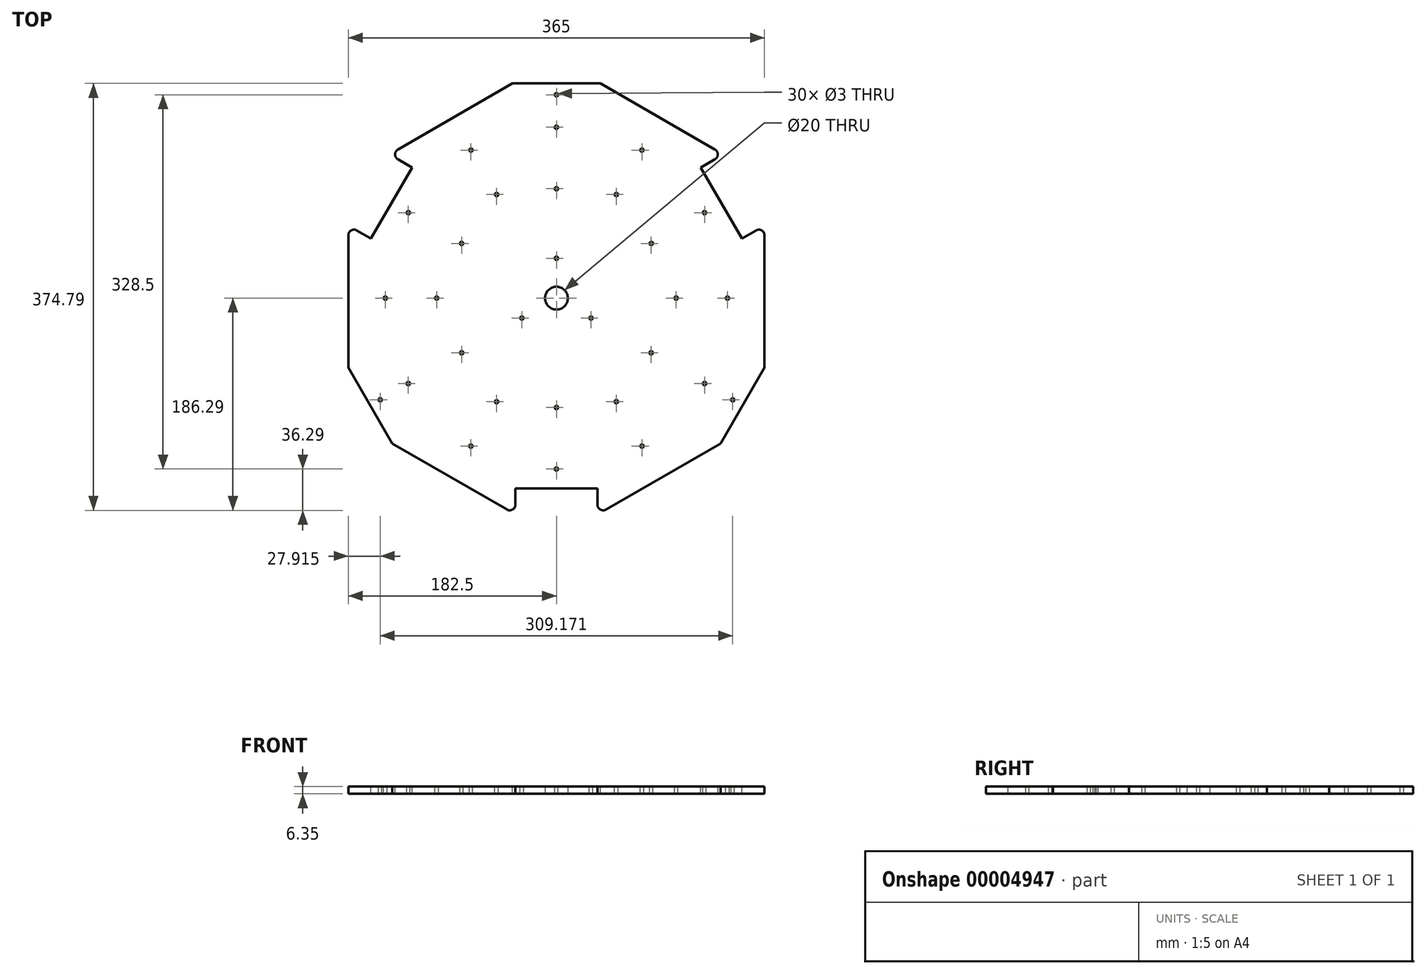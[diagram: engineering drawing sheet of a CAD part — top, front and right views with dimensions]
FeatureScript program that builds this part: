
annotation { "Feature Type Name" : "Feature", "Feature Type Description" : "" }
export const myFeature = defineFeature(function(context is Context, id is Id, definition is map)
    precondition{}
    {
        {
            var Q0;
            Q0=qCreatedBy(makeId("Top.planeOp"),FACE);
            var sketch = newSketch(context, id + "F0", { "sketchPlane" : qUnion([Q0])});
            skCircle(sketch, "E0", {"center": v(0, 0) * mm, "radius": 210.73 * mm, "construction": true});
            skLineSegment(sketch, "E1", {"start": v(0, 210.73) * mm, "end": v(0, 0) * mm, "construction": true});
            skLineSegment(sketch, "E2", {"start": v(0, 0) * mm, "end": v(-182.5, 105.37) * mm, "construction": true});
            skLineSegment(sketch, "E3", {"start": v(-182.5, 105.37) * mm, "end": v(0, 210.73) * mm});
            skLineSegment(sketch, "E4.1.0", {"start": v(-182.5, -105.37) * mm, "end": v(-182.5, 105.37) * mm});
            skLineSegment(sketch, "E4.2.0", {"start": v(0, -210.73) * mm, "end": v(-182.5, -105.37) * mm});
            skLineSegment(sketch, "E4.3.0", {"start": v(182.5, -105.37) * mm, "end": v(0, -210.73) * mm});
            skLineSegment(sketch, "E4.4.0", {"start": v(182.5, 105.37) * mm, "end": v(182.5, -105.37) * mm});
            skLineSegment(sketch, "E4.5.0", {"start": v(0, 210.73) * mm, "end": v(182.5, 105.37) * mm});
            skCircle(sketch, "E5", {"center": v(0, 0) * mm, "radius": 10 * mm});
            skSolve(sketch);
        }
        {
            var Q0;
            Q0 = qSketchRegion(id + "F0", true);
            extrude(context, id + "F1", {"entities" : qUnion([Q0]), "depth" : 6.35 * mm});
        }
        {
            var Q0;
            Q0=makeQuery(id+"F1.opExtrude","CAP_FACE",FACE,{"disambiguationData":[OSD([sQuery(id+"F0.wireOp",EDGE,"E3"),sQuery(id+"F0.wireOp",EDGE,"E4.1.0"),sQuery(id+"F0.wireOp",EDGE,"E4.2.0"),sQuery(id+"F0.wireOp",EDGE,"E4.3.0"),sQuery(id+"F0.wireOp",EDGE,"E4.4.0"),sQuery(id+"F0.wireOp",EDGE,"E4.5.0"),sQuery(id+"F0.wireOp",EDGE,"E5")])],"isStart":false});
            var sketch = newSketch(context, id + "F2", { "sketchPlane" : qUnion([Q0])});
            skLineSegment(sketch, "E6", {"start": v(0, 0) * mm, "end": v(182.5, 0) * mm, "construction": true});
            skLineSegment(sketch, "E7", {"start": v(-38.5, 188.5) * mm, "end": v(38.5, 188.5) * mm});
            skPoint(sketch, "E8", {"position": v(0, 188.5) * mm});
            skLineSegment(sketch, "E9", {"start": v(-38.5, 188.5) * mm, "end": v(0, 210.73) * mm});
            skLineSegment(sketch, "E10", {"start": v(0, 210.73) * mm, "end": v(38.5, 188.5) * mm});
            skLineSegment(sketch, "E11.1.0", {"start": v(-182.5, 60.9) * mm, "end": v(-182.5, 105.37) * mm});
            skLineSegment(sketch, "E11.1.1", {"start": v(-182.5, 105.37) * mm, "end": v(-144, 127.6) * mm});
            skLineSegment(sketch, "E11.1.2", {"start": v(-182.5, 60.9) * mm, "end": v(-144, 127.6) * mm});
            skPoint(sketch, "E11.1.3", {"position": v(-163.25, 94.25) * mm});
            skLineSegment(sketch, "E11.2.0", {"start": v(-144, -127.6) * mm, "end": v(-182.5, -105.37) * mm});
            skLineSegment(sketch, "E11.2.1", {"start": v(-182.5, -105.37) * mm, "end": v(-182.5, -60.9) * mm});
            skLineSegment(sketch, "E11.2.2", {"start": v(-144, -127.6) * mm, "end": v(-182.5, -60.9) * mm});
            skPoint(sketch, "E11.2.3", {"position": v(-163.25, -94.25) * mm});
            skLineSegment(sketch, "E11.3.0", {"start": v(38.5, -188.5) * mm, "end": v(0, -210.73) * mm});
            skLineSegment(sketch, "E11.3.1", {"start": v(0, -210.73) * mm, "end": v(-38.5, -188.5) * mm});
            skLineSegment(sketch, "E11.3.2", {"start": v(38.5, -188.5) * mm, "end": v(-38.5, -188.5) * mm});
            skPoint(sketch, "E11.3.3", {"position": v(0, -188.5) * mm});
            skLineSegment(sketch, "E11.4.0", {"start": v(182.5, -60.9) * mm, "end": v(182.5, -105.37) * mm});
            skLineSegment(sketch, "E11.4.1", {"start": v(182.5, -105.37) * mm, "end": v(144, -127.6) * mm});
            skLineSegment(sketch, "E11.4.2", {"start": v(182.5, -60.9) * mm, "end": v(144, -127.6) * mm});
            skPoint(sketch, "E11.4.3", {"position": v(163.25, -94.25) * mm});
            skLineSegment(sketch, "E11.5.0", {"start": v(144, 127.6) * mm, "end": v(182.5, 105.37) * mm});
            skLineSegment(sketch, "E11.5.1", {"start": v(182.5, 105.37) * mm, "end": v(182.5, 60.9) * mm});
            skLineSegment(sketch, "E11.5.2", {"start": v(144, 127.6) * mm, "end": v(182.5, 60.9) * mm});
            skPoint(sketch, "E11.5.3", {"position": v(163.25, 94.25) * mm});
            skPoint(sketch, "E11.center", {"position": v(0, 0) * mm});
            skSolve(sketch);
        }
        {
            var Q0;
            Q0 = qSketchRegion(id + "F2", true);
            extrude(context, id + "F3", {"entities" : qUnion([Q0]), "operationType" : NewBodyOperationType.REMOVE, "endBound" : BoundingType.THROUGH_ALL, "oppositeDirection" : true, "depth" : 25 * mm});
        }
        {
            var Q0;
            Q0=makeQuery(id+"F1.opExtrude","CAP_FACE",FACE,{"disambiguationData":[OSD([sQuery(id+"F0.wireOp",EDGE,"E3"),sQuery(id+"F0.wireOp",EDGE,"E4.1.0"),sQuery(id+"F0.wireOp",EDGE,"E4.2.0"),sQuery(id+"F0.wireOp",EDGE,"E4.3.0"),sQuery(id+"F0.wireOp",EDGE,"E4.4.0"),sQuery(id+"F0.wireOp",EDGE,"E4.5.0"),sQuery(id+"F0.wireOp",EDGE,"E5")])],"isStart":false});
            var sketch = newSketch(context, id + "F4", { "sketchPlane" : qUnion([Q0])});
            skLineSegment(sketch, "E12", {"start": v(0, 188.5) * mm, "end": v(0, 0) * mm, "construction": true});
            skLineSegment(sketch, "E13", {"start": v(0, 0) * mm, "end": v(-163.25, -94.25) * mm, "construction": true});
            skLineSegment(sketch, "E14", {"start": v(0, 0) * mm, "end": v(163.25, -94.25) * mm, "construction": true});
            skCircle(sketch, "E15", {"center": v(0, 178.5) * mm, "radius": 1.5 * mm});
            skCircle(sketch, "E16", {"center": v(0, 35) * mm, "radius": 1.5 * mm});
            skCircle(sketch, "E17", {"center": v(0, 0) * mm, "radius": 25 * mm, "construction": true});
            skPoint(sketch, "E18", {"position": v(0, 25) * mm});
            skCircle(sketch, "E19.1.0", {"center": v(-30.31, -17.5) * mm, "radius": 1.5 * mm});
            skCircle(sketch, "E19.1.1", {"center": v(-154.59, -89.25) * mm, "radius": 1.5 * mm});
            skCircle(sketch, "E19.2.0", {"center": v(30.31, -17.5) * mm, "radius": 1.5 * mm});
            skCircle(sketch, "E19.2.1", {"center": v(154.59, -89.25) * mm, "radius": 1.5 * mm});
            skSolve(sketch);
        }
        {
            var Q0;
            Q0 = qSketchRegion(id + "F4", true);
            extrude(context, id + "F5", {"entities" : qUnion([Q0]), "operationType" : NewBodyOperationType.REMOVE, "endBound" : BoundingType.THROUGH_ALL, "oppositeDirection" : true, "depth" : 25 * mm});
        }
        {
            var Q0;
            Q0=makeQuery(id+"F1.opExtrude","CAP_FACE",FACE,{"disambiguationData":[OSD([sQuery(id+"F0.wireOp",EDGE,"E3"),sQuery(id+"F0.wireOp",EDGE,"E4.1.0"),sQuery(id+"F0.wireOp",EDGE,"E4.2.0"),sQuery(id+"F0.wireOp",EDGE,"E4.3.0"),sQuery(id+"F0.wireOp",EDGE,"E4.4.0"),sQuery(id+"F0.wireOp",EDGE,"E4.5.0"),sQuery(id+"F0.wireOp",EDGE,"E5")])],"isStart":false});
            var sketch = newSketch(context, id + "F6", { "sketchPlane" : qUnion([Q0])});
            skLineSegment(sketch, "E20", {"start": v(0, 0) * mm, "end": v(163.25, 94.25) * mm, "construction": true});
            skLineSegment(sketch, "E21", {"start": v(106.75, 149.1) * mm, "end": v(182.5, 17.9) * mm});
            skLineSegment(sketch, "E22.0", {"start": v(144, 127.6) * mm, "end": v(182.5, 60.9) * mm});
            skLineSegment(sketch, "E23", {"start": v(106.75, 149.1) * mm, "end": v(144, 127.6) * mm});
            skLineSegment(sketch, "E24", {"start": v(182.5, 60.9) * mm, "end": v(182.5, 17.9) * mm});
            skLineSegment(sketch, "E25.1.0", {"start": v(-144, 127.6) * mm, "end": v(-106.75, 149.1) * mm});
            skLineSegment(sketch, "E25.1.1", {"start": v(-182.5, 17.9) * mm, "end": v(-182.5, 60.9) * mm});
            skLineSegment(sketch, "E25.1.2", {"start": v(-182.5, 17.9) * mm, "end": v(-106.75, 149.1) * mm});
            skLineSegment(sketch, "E25.1.3", {"start": v(-182.5, 60.9) * mm, "end": v(-144, 127.6) * mm});
            skLineSegment(sketch, "E25.2.0", {"start": v(-38.5, -188.5) * mm, "end": v(-75.75, -167) * mm});
            skLineSegment(sketch, "E25.2.1", {"start": v(75.75, -167) * mm, "end": v(38.5, -188.5) * mm});
            skLineSegment(sketch, "E25.2.2", {"start": v(75.75, -167) * mm, "end": v(-75.75, -167) * mm});
            skLineSegment(sketch, "E25.2.3", {"start": v(38.5, -188.5) * mm, "end": v(-38.5, -188.5) * mm});
            skPoint(sketch, "E25.center", {"position": v(0, 0) * mm});
            skSolve(sketch);
        }
        {
            var Q0;
            Q0 = qSketchRegion(id + "F6", true);
            extrude(context, id + "F7", {"entities" : qUnion([Q0]), "operationType" : NewBodyOperationType.REMOVE, "endBound" : BoundingType.THROUGH_ALL, "oppositeDirection" : true, "depth" : 25 * mm});
        }
        {
            var Q0;
            Q0=makeQuery(id+"F1.opExtrude","CAP_FACE",FACE,{"disambiguationData":[OSD([sQuery(id+"F0.wireOp",EDGE,"E3"),sQuery(id+"F0.wireOp",EDGE,"E4.1.0"),sQuery(id+"F0.wireOp",EDGE,"E4.2.0"),sQuery(id+"F0.wireOp",EDGE,"E4.3.0"),sQuery(id+"F0.wireOp",EDGE,"E4.4.0"),sQuery(id+"F0.wireOp",EDGE,"E4.5.0"),sQuery(id+"F0.wireOp",EDGE,"E5")])],"isStart":false});
            var sketch = newSketch(context, id + "F8", { "sketchPlane" : qUnion([Q0])});
            skLineSegment(sketch, "E26", {"start": v(0, 0) * mm, "end": v(144.63, 83.5) * mm, "construction": true});
            skLineSegment(sketch, "E27", {"start": v(106.75, 149.1) * mm, "end": v(146.5, 126.15) * mm});
            skLineSegment(sketch, "E28", {"start": v(146.5, 126.15) * mm, "end": v(126.63, 114.68) * mm});
            skLineSegment(sketch, "E29", {"start": v(126.63, 114.68) * mm, "end": v(106.75, 149.1) * mm});
            skLineSegment(sketch, "E30.0.MirrorCS", {"start": v(182.5, 17.9) * mm, "end": v(182.5, 63.8) * mm});
            skLineSegment(sketch, "E30.1.MirrorCS", {"start": v(162.63, 52.32) * mm, "end": v(182.5, 17.9) * mm});
            skLineSegment(sketch, "E30.2.MirrorCS", {"start": v(182.5, 63.8) * mm, "end": v(162.63, 52.32) * mm});
            skLineSegment(sketch, "E31.1.0", {"start": v(-162.63, 52.32) * mm, "end": v(-182.5, 17.9) * mm});
            skLineSegment(sketch, "E31.1.1", {"start": v(-182.5, 17.9) * mm, "end": v(-182.5, 63.8) * mm});
            skLineSegment(sketch, "E31.1.2", {"start": v(-182.5, 63.8) * mm, "end": v(-162.63, 52.32) * mm});
            skLineSegment(sketch, "E31.1.3", {"start": v(-106.75, 149.1) * mm, "end": v(-146.5, 126.15) * mm});
            skLineSegment(sketch, "E31.1.4", {"start": v(-126.63, 114.68) * mm, "end": v(-106.75, 149.1) * mm});
            skLineSegment(sketch, "E31.1.5", {"start": v(-146.5, 126.15) * mm, "end": v(-126.63, 114.68) * mm});
            skLineSegment(sketch, "E31.2.0", {"start": v(36, -167) * mm, "end": v(75.75, -167) * mm});
            skLineSegment(sketch, "E31.2.1", {"start": v(75.75, -167) * mm, "end": v(36, -189.95) * mm});
            skLineSegment(sketch, "E31.2.2", {"start": v(36, -189.95) * mm, "end": v(36, -167) * mm});
            skLineSegment(sketch, "E31.2.3", {"start": v(-75.75, -167) * mm, "end": v(-36, -189.95) * mm});
            skLineSegment(sketch, "E31.2.4", {"start": v(-36, -167) * mm, "end": v(-75.75, -167) * mm});
            skLineSegment(sketch, "E31.2.5", {"start": v(-36, -189.95) * mm, "end": v(-36, -167) * mm});
            skPoint(sketch, "E31.center", {"position": v(0, 0) * mm});
            skSolve(sketch);
        }
        {
            var Q0;
            Q0 = qSketchRegion(id + "F8", true);
            var Q1;
            Q1=makeQuery(id+"F1.opExtrude","CAP_FACE",FACE,{"disambiguationData":[OSD([sQuery(id+"F0.wireOp",EDGE,"E3"),sQuery(id+"F0.wireOp",EDGE,"E4.1.0"),sQuery(id+"F0.wireOp",EDGE,"E4.2.0"),sQuery(id+"F0.wireOp",EDGE,"E4.3.0"),sQuery(id+"F0.wireOp",EDGE,"E4.4.0"),sQuery(id+"F0.wireOp",EDGE,"E4.5.0"),sQuery(id+"F0.wireOp",EDGE,"E5")])],"isStart":true});
            extrude(context, id + "F9", {"entities" : qUnion([Q0]), "operationType" : NewBodyOperationType.ADD, "endBound" : BoundingType.UP_TO_SURFACE, "oppositeDirection" : true, "endBoundEntityFace" : qUnion([Q1]), "depth" : 25 * mm});
        }
        {
            var Q0;
            Q0=makeQuery(id+"F9.opExtrude","SWEPT_EDGE",EDGE,{"disambiguationData":[OSD([sQuery(id+"F8.wireOp",EDGE,"E31.2.3"),sQuery(id+"F8.wireOp",EDGE,"E31.2.5")])]});
            var Q1;
            Q1=makeQuery(id+"F9.opExtrude","SWEPT_EDGE",EDGE,{"disambiguationData":[OSD([sQuery(id+"F6.wireOp",EDGE,"E25.2.2"),sQuery(id+"F8.wireOp",EDGE,"E31.2.4"),sQuery(id+"F8.wireOp",EDGE,"E31.2.5")])]});
            var Q2;
            Q2=makeQuery(id+"F9.opExtrude","SWEPT_EDGE",EDGE,{"disambiguationData":[OSD([sQuery(id+"F6.wireOp",EDGE,"E25.2.2"),sQuery(id+"F8.wireOp",EDGE,"E31.2.0"),sQuery(id+"F8.wireOp",EDGE,"E31.2.2")])]});
            var Q3;
            Q3=makeQuery(id+"F9.opExtrude","SWEPT_EDGE",EDGE,{"disambiguationData":[OSD([sQuery(id+"F8.wireOp",EDGE,"E31.2.1"),sQuery(id+"F8.wireOp",EDGE,"E31.2.2")])]});
            var Q4;
            Q4=makeQuery(id+"F3.boolean.opBoolean","COPY",EDGE,{"derivedFrom":makeQuery(id+"F3.opExtrude","SWEPT_EDGE",EDGE,{"disambiguationData":[OSD([sQuery(id+"F0.wireOp",EDGE,"E4.3.0"),sQuery(id+"F2.wireOp",EDGE,"E11.4.1"),sQuery(id+"F2.wireOp",EDGE,"E11.4.2")])]})});
            var Q5;
            Q5=makeQuery(id+"F3.boolean.opBoolean","COPY",EDGE,{"derivedFrom":makeQuery(id+"F3.opExtrude","SWEPT_EDGE",EDGE,{"disambiguationData":[OSD([sQuery(id+"F0.wireOp",EDGE,"E4.4.0"),sQuery(id+"F2.wireOp",EDGE,"E11.4.0"),sQuery(id+"F2.wireOp",EDGE,"E11.4.2")])]})});
            var Q6;
            Q6=makeQuery(id+"F9.opExtrude","SWEPT_EDGE",EDGE,{"disambiguationData":[OSD([sQuery(id+"F8.wireOp",EDGE,"E30.0.MirrorCS"),sQuery(id+"F8.wireOp",EDGE,"E30.2.MirrorCS")])]});
            var Q7;
            Q7=makeQuery(id+"F9.opExtrude","SWEPT_EDGE",EDGE,{"disambiguationData":[OSD([sQuery(id+"F8.wireOp",EDGE,"E27"),sQuery(id+"F8.wireOp",EDGE,"E28")])]});
            var Q8;
            Q8=makeQuery(id+"F9.opExtrude","SWEPT_EDGE",EDGE,{"disambiguationData":[OSD([sQuery(id+"F6.wireOp",EDGE,"E21"),sQuery(id+"F8.wireOp",EDGE,"E28"),sQuery(id+"F8.wireOp",EDGE,"E29")])]});
            var Q9;
            Q9=makeQuery(id+"F9.opExtrude","SWEPT_EDGE",EDGE,{"disambiguationData":[OSD([sQuery(id+"F6.wireOp",EDGE,"E21"),sQuery(id+"F8.wireOp",EDGE,"E30.1.MirrorCS"),sQuery(id+"F8.wireOp",EDGE,"E30.2.MirrorCS")])]});
            var Q10;
            Q10=makeQuery(id+"F3.boolean.opBoolean","COPY",EDGE,{"derivedFrom":makeQuery(id+"F3.opExtrude","SWEPT_EDGE",EDGE,{"disambiguationData":[OSD([sQuery(id+"F0.wireOp",EDGE,"E3"),sQuery(id+"F2.wireOp",EDGE,"E7"),sQuery(id+"F2.wireOp",EDGE,"E9")])]})});
            var Q11;
            Q11=makeQuery(id+"F3.boolean.opBoolean","COPY",EDGE,{"derivedFrom":makeQuery(id+"F3.opExtrude","SWEPT_EDGE",EDGE,{"disambiguationData":[OSD([sQuery(id+"F0.wireOp",EDGE,"E4.5.0"),sQuery(id+"F2.wireOp",EDGE,"E7"),sQuery(id+"F2.wireOp",EDGE,"E10")])]})});
            var Q12;
            Q12=makeQuery(id+"F9.opExtrude","SWEPT_EDGE",EDGE,{"disambiguationData":[OSD([sQuery(id+"F8.wireOp",EDGE,"E31.1.1"),sQuery(id+"F8.wireOp",EDGE,"E31.1.2")])]});
            var Q13;
            Q13=makeQuery(id+"F9.opExtrude","SWEPT_EDGE",EDGE,{"disambiguationData":[OSD([sQuery(id+"F6.wireOp",EDGE,"E25.1.2"),sQuery(id+"F8.wireOp",EDGE,"E31.1.0"),sQuery(id+"F8.wireOp",EDGE,"E31.1.2")])]});
            var Q14;
            Q14=makeQuery(id+"F9.opExtrude","SWEPT_EDGE",EDGE,{"disambiguationData":[OSD([sQuery(id+"F6.wireOp",EDGE,"E25.1.2"),sQuery(id+"F8.wireOp",EDGE,"E31.1.4"),sQuery(id+"F8.wireOp",EDGE,"E31.1.5")])]});
            var Q15;
            Q15=makeQuery(id+"F9.opExtrude","SWEPT_EDGE",EDGE,{"disambiguationData":[OSD([sQuery(id+"F8.wireOp",EDGE,"E31.1.3"),sQuery(id+"F8.wireOp",EDGE,"E31.1.5")])]});
            var Q16;
            Q16=makeQuery(id+"F3.boolean.opBoolean","COPY",EDGE,{"derivedFrom":makeQuery(id+"F3.opExtrude","SWEPT_EDGE",EDGE,{"disambiguationData":[OSD([sQuery(id+"F0.wireOp",EDGE,"E4.1.0"),sQuery(id+"F2.wireOp",EDGE,"E11.2.1"),sQuery(id+"F2.wireOp",EDGE,"E11.2.2")])]})});
            var Q17;
            Q17=makeQuery(id+"F3.boolean.opBoolean","COPY",EDGE,{"derivedFrom":makeQuery(id+"F3.opExtrude","SWEPT_EDGE",EDGE,{"disambiguationData":[OSD([sQuery(id+"F0.wireOp",EDGE,"E4.2.0"),sQuery(id+"F2.wireOp",EDGE,"E11.2.0"),sQuery(id+"F2.wireOp",EDGE,"E11.2.2")])]})});
            fillet(context, id + "F10", {"entities" : qUnion([Q0, Q1, Q2, Q3, Q4, Q5, Q6, Q7, Q8, Q9, Q10, Q11, Q12, Q13, Q14, Q15, Q16, Q17]), "radius" : 5 * mm, "tangentPropagation" : true, "allowEdgeOverflow" : false});
        }
        {
            var Q0;
            Q0=makeQuery(id+"F1.opExtrude","CAP_FACE",FACE,{"disambiguationData":[OSD([sQuery(id+"F0.wireOp",EDGE,"E3"),sQuery(id+"F0.wireOp",EDGE,"E4.1.0"),sQuery(id+"F0.wireOp",EDGE,"E4.2.0"),sQuery(id+"F0.wireOp",EDGE,"E4.3.0"),sQuery(id+"F0.wireOp",EDGE,"E4.4.0"),sQuery(id+"F0.wireOp",EDGE,"E4.5.0"),sQuery(id+"F0.wireOp",EDGE,"E5")])],"isStart":false});
            var sketch = newSketch(context, id + "F11", { "sketchPlane" : qUnion([Q0])});
            skLineSegment(sketch, "E32", {"start": v(0, 188.5) * mm, "end": v(0, 0) * mm, "construction": true});
            skCircle(sketch, "E33", {"center": v(0, 96) * mm, "radius": 1.5 * mm});
            skCircle(sketch, "E34.1.0", {"center": v(-83.14, 48) * mm, "radius": 1.5 * mm});
            skCircle(sketch, "E34.2.0", {"center": v(-83.14, -48) * mm, "radius": 1.5 * mm});
            skCircle(sketch, "E34.3.0", {"center": v(0, -96) * mm, "radius": 1.5 * mm});
            skCircle(sketch, "E34.4.0", {"center": v(83.14, -48) * mm, "radius": 1.5 * mm});
            skCircle(sketch, "E34.5.0", {"center": v(83.14, 48) * mm, "radius": 1.5 * mm});
            skPoint(sketch, "E34.center", {"position": v(0, 0) * mm});
            skSolve(sketch);
        }
        {
            var Q0;
            Q0 = qSketchRegion(id + "F11", true);
            extrude(context, id + "F12", {"entities" : qUnion([Q0]), "operationType" : NewBodyOperationType.REMOVE, "endBound" : BoundingType.THROUGH_ALL, "oppositeDirection" : true, "depth" : 25 * mm});
        }
        {
            var Q0;
            Q0=makeQuery(id+"F9.boolean.opBoolean","MERGE",FACE,{"derivedFrom":[makeQuery(id+"F1.opExtrude","CAP_FACE",FACE,{"disambiguationData":[OSD([sQuery(id+"F0.wireOp",EDGE,"E3"),sQuery(id+"F0.wireOp",EDGE,"E4.1.0"),sQuery(id+"F0.wireOp",EDGE,"E4.2.0"),sQuery(id+"F0.wireOp",EDGE,"E4.3.0"),sQuery(id+"F0.wireOp",EDGE,"E4.4.0"),sQuery(id+"F0.wireOp",EDGE,"E4.5.0"),sQuery(id+"F0.wireOp",EDGE,"E5")])],"isStart":false}),makeQuery(id+"F9.opExtrude","CAP_FACE",FACE,{"disambiguationData":[OSD([sQuery(id+"F8.wireOp",EDGE,"E27"),sQuery(id+"F8.wireOp",EDGE,"E28"),sQuery(id+"F8.wireOp",EDGE,"E29")])],"isStart":true}),makeQuery(id+"F9.opExtrude","CAP_FACE",FACE,{"disambiguationData":[OSD([sQuery(id+"F8.wireOp",EDGE,"E30.0.MirrorCS"),sQuery(id+"F8.wireOp",EDGE,"E30.1.MirrorCS"),sQuery(id+"F8.wireOp",EDGE,"E30.2.MirrorCS")])],"isStart":true}),makeQuery(id+"F9.opExtrude","CAP_FACE",FACE,{"disambiguationData":[OSD([sQuery(id+"F8.wireOp",EDGE,"E31.1.0"),sQuery(id+"F8.wireOp",EDGE,"E31.1.1"),sQuery(id+"F8.wireOp",EDGE,"E31.1.2")])],"isStart":true}),makeQuery(id+"F9.opExtrude","CAP_FACE",FACE,{"disambiguationData":[OSD([sQuery(id+"F8.wireOp",EDGE,"E31.1.3"),sQuery(id+"F8.wireOp",EDGE,"E31.1.4"),sQuery(id+"F8.wireOp",EDGE,"E31.1.5")])],"isStart":true}),makeQuery(id+"F9.opExtrude","CAP_FACE",FACE,{"disambiguationData":[OSD([sQuery(id+"F8.wireOp",EDGE,"E31.2.0"),sQuery(id+"F8.wireOp",EDGE,"E31.2.1"),sQuery(id+"F8.wireOp",EDGE,"E31.2.2")])],"isStart":true}),makeQuery(id+"F9.opExtrude","CAP_FACE",FACE,{"disambiguationData":[OSD([sQuery(id+"F8.wireOp",EDGE,"E31.2.3"),sQuery(id+"F8.wireOp",EDGE,"E31.2.4"),sQuery(id+"F8.wireOp",EDGE,"E31.2.5")])],"isStart":true})]});
            var sketch = newSketch(context, id + "F13", { "sketchPlane" : qUnion([Q0])});
            skCircle(sketch, "E35", {"center": v(0, 0) * mm, "radius": 150 * mm, "construction": true});
            skLineSegment(sketch, "E36", {"start": v(0, 0) * mm, "end": v(0, 150) * mm, "construction": true});
            skCircle(sketch, "E37", {"center": v(0, 150) * mm, "radius": 1.5 * mm});
            skCircle(sketch, "E38.1.0", {"center": v(-75, 129.9) * mm, "radius": 1.5 * mm});
            skCircle(sketch, "E38.2.0", {"center": v(-129.9, 75) * mm, "radius": 1.5 * mm});
            skCircle(sketch, "E38.3.0", {"center": v(-150, 0) * mm, "radius": 1.5 * mm});
            skCircle(sketch, "E38.4.0", {"center": v(-129.9, -75) * mm, "radius": 1.5 * mm});
            skCircle(sketch, "E38.5.0", {"center": v(-75, -129.9) * mm, "radius": 1.5 * mm});
            skCircle(sketch, "E38.6.0", {"center": v(0, -150) * mm, "radius": 1.5 * mm});
            skCircle(sketch, "E38.7.0", {"center": v(75, -129.9) * mm, "radius": 1.5 * mm});
            skCircle(sketch, "E38.8.0", {"center": v(129.9, -75) * mm, "radius": 1.5 * mm});
            skCircle(sketch, "E38.9.0", {"center": v(150, 0) * mm, "radius": 1.5 * mm});
            skCircle(sketch, "E38.10.0", {"center": v(129.9, 75) * mm, "radius": 1.5 * mm});
            skCircle(sketch, "E38.11.0", {"center": v(75, 129.9) * mm, "radius": 1.5 * mm});
            skSolve(sketch);
        }
        {
            var Q0;
            Q0 = qSketchRegion(id + "F13", true);
            extrude(context, id + "F14", {"entities" : qUnion([Q0]), "operationType" : NewBodyOperationType.REMOVE, "endBound" : BoundingType.THROUGH_ALL, "oppositeDirection" : true, "depth" : 25 * mm});
        }
        {
            var Q0;
            Q0=makeQuery(id+"F9.boolean.opBoolean","MERGE",FACE,{"derivedFrom":[makeQuery(id+"F1.opExtrude","CAP_FACE",FACE,{"disambiguationData":[OSD([sQuery(id+"F0.wireOp",EDGE,"E3"),sQuery(id+"F0.wireOp",EDGE,"E4.1.0"),sQuery(id+"F0.wireOp",EDGE,"E4.2.0"),sQuery(id+"F0.wireOp",EDGE,"E4.3.0"),sQuery(id+"F0.wireOp",EDGE,"E4.4.0"),sQuery(id+"F0.wireOp",EDGE,"E4.5.0"),sQuery(id+"F0.wireOp",EDGE,"E5")])],"isStart":false}),makeQuery(id+"F9.opExtrude","CAP_FACE",FACE,{"disambiguationData":[OSD([sQuery(id+"F8.wireOp",EDGE,"E27"),sQuery(id+"F8.wireOp",EDGE,"E28"),sQuery(id+"F8.wireOp",EDGE,"E29")])],"isStart":true}),makeQuery(id+"F9.opExtrude","CAP_FACE",FACE,{"disambiguationData":[OSD([sQuery(id+"F8.wireOp",EDGE,"E30.0.MirrorCS"),sQuery(id+"F8.wireOp",EDGE,"E30.1.MirrorCS"),sQuery(id+"F8.wireOp",EDGE,"E30.2.MirrorCS")])],"isStart":true}),makeQuery(id+"F9.opExtrude","CAP_FACE",FACE,{"disambiguationData":[OSD([sQuery(id+"F8.wireOp",EDGE,"E31.1.0"),sQuery(id+"F8.wireOp",EDGE,"E31.1.1"),sQuery(id+"F8.wireOp",EDGE,"E31.1.2")])],"isStart":true}),makeQuery(id+"F9.opExtrude","CAP_FACE",FACE,{"disambiguationData":[OSD([sQuery(id+"F8.wireOp",EDGE,"E31.1.3"),sQuery(id+"F8.wireOp",EDGE,"E31.1.4"),sQuery(id+"F8.wireOp",EDGE,"E31.1.5")])],"isStart":true}),makeQuery(id+"F9.opExtrude","CAP_FACE",FACE,{"disambiguationData":[OSD([sQuery(id+"F8.wireOp",EDGE,"E31.2.0"),sQuery(id+"F8.wireOp",EDGE,"E31.2.1"),sQuery(id+"F8.wireOp",EDGE,"E31.2.2")])],"isStart":true}),makeQuery(id+"F9.opExtrude","CAP_FACE",FACE,{"disambiguationData":[OSD([sQuery(id+"F8.wireOp",EDGE,"E31.2.3"),sQuery(id+"F8.wireOp",EDGE,"E31.2.4"),sQuery(id+"F8.wireOp",EDGE,"E31.2.5")])],"isStart":true})]});
            var sketch = newSketch(context, id + "F15", { "sketchPlane" : qUnion([Q0])});
            skCircle(sketch, "E39", {"center": v(0, 0) * mm, "radius": 105 * mm, "construction": true});
            skLineSegment(sketch, "E40", {"start": v(0, 0) * mm, "end": v(-75, 129.9) * mm, "construction": true});
            skCircle(sketch, "E41", {"center": v(-52.5, 90.93) * mm, "radius": 1.5 * mm});
            skCircle(sketch, "E42.1.0", {"center": v(-105, 0) * mm, "radius": 1.5 * mm});
            skCircle(sketch, "E42.2.0", {"center": v(-52.5, -90.93) * mm, "radius": 1.5 * mm});
            skCircle(sketch, "E42.3.0", {"center": v(52.5, -90.93) * mm, "radius": 1.5 * mm});
            skCircle(sketch, "E42.4.0", {"center": v(105, 0) * mm, "radius": 1.5 * mm});
            skCircle(sketch, "E42.5.0", {"center": v(52.5, 90.93) * mm, "radius": 1.5 * mm});
            skSolve(sketch);
        }
        {
            var Q0;
            Q0 = qSketchRegion(id + "F15", true);
            extrude(context, id + "F16", {"entities" : qUnion([Q0]), "operationType" : NewBodyOperationType.REMOVE, "endBound" : BoundingType.THROUGH_ALL, "oppositeDirection" : true, "depth" : 25 * mm});
        }
    });
